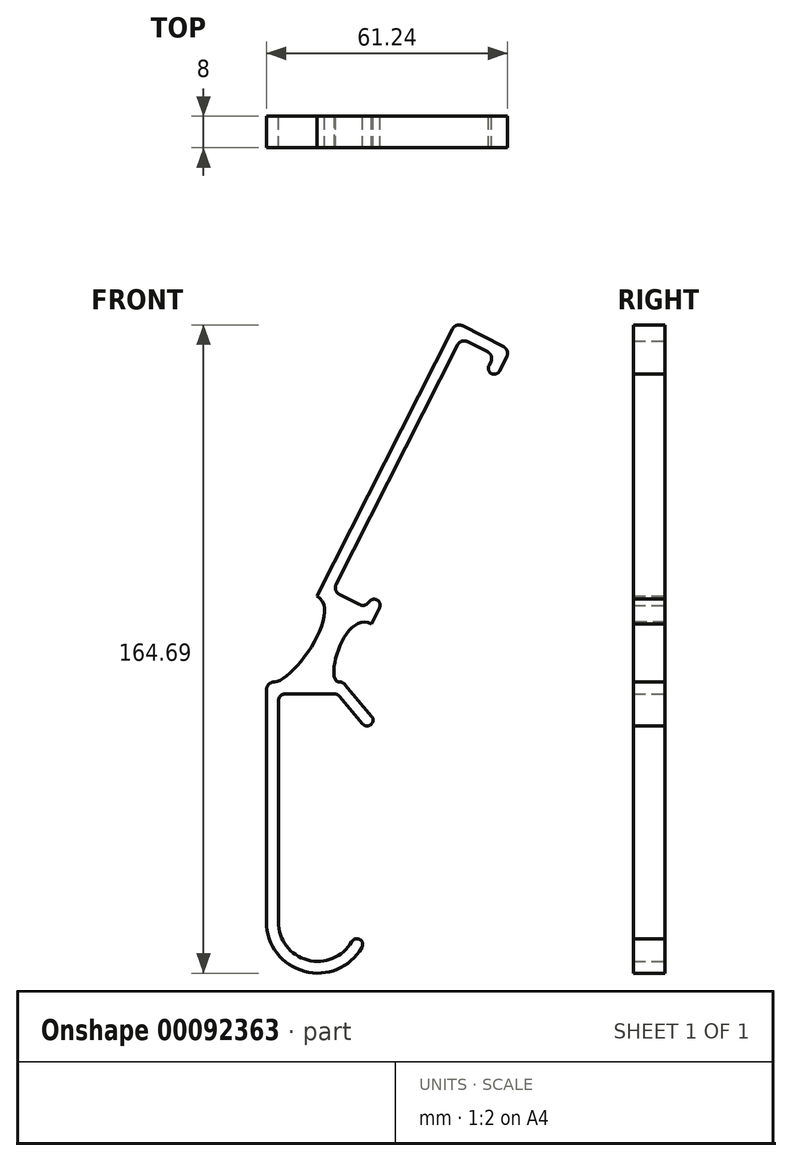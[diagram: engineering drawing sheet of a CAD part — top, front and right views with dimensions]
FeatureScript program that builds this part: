
annotation { "Feature Type Name" : "Feature", "Feature Type Description" : "" }
export const myFeature = defineFeature(function(context is Context, id is Id, definition is map)
    precondition{}
    {
        {
            var Q0;
            Q0=qCreatedBy(makeId("Front.planeOp"),FACE);
            var sketch = newSketch(context, id + "F0", { "sketchPlane" : qUnion([Q0])});
            skLineSegment(sketch, "E0", {"start": v(0, -2) * mm, "end": v(0, -58) * mm});
            skLineSegment(sketch, "E1", {"start": v(2, 0) * mm, "end": v(14.07, 0) * mm});
            skLineSegment(sketch, "E2", {"start": v(15.6, -0.71) * mm, "end": v(21.43, -7.66) * mm});
            skArc(sketch, "E3", {"start": v(0, -58) * mm, "mid": v(7.41, -67.66) * mm, "end": v(18.66, -63) * mm});
            skArc(sketch, "E4.0", {"start": v(-3, -58) * mm, "mid": v(6.64, -70.56) * mm, "end": v(21.26, -64.5) * mm});
            skLineSegment(sketch, "E4.1", {"start": v(-3, 1) * mm, "end": v(-3, -58) * mm});
            skLineSegment(sketch, "E4.2", {"start": v(-1, 3) * mm, "end": v(15.47, 3) * mm});
            skLineSegment(sketch, "E4.3", {"start": v(17, 2.29) * mm, "end": v(23.73, -5.73) * mm});
            skArc(sketch, "E5", {"start": v(21.43, -7.66) * mm, "mid": v(23.54, -7.85) * mm, "end": v(23.73, -5.73) * mm});
            skArc(sketch, "E6", {"start": v(21.26, -64.5) * mm, "mid": v(20.7, -62.45) * mm, "end": v(18.66, -63) * mm});
            skPoint(sketch, "E7.visualSharp", {"position": v(0, 0) * mm});
            skArc(sketch, "E7.filletArc", {"start": v(2, 0) * mm, "mid": v(0.59, -0.59) * mm, "end": v(0, -2) * mm});
            skPoint(sketch, "E8.visualSharp", {"position": v(15, 0) * mm});
            skArc(sketch, "E8.filletArc", {"start": v(15.6, -0.71) * mm, "mid": v(14.91, -0.19) * mm, "end": v(14.07, 0) * mm});
            skArc(sketch, "E9.filletArc", {"start": v(17, 2.29) * mm, "mid": v(16.31, 2.81) * mm, "end": v(15.47, 3) * mm});
            skPoint(sketch, "E10.visualSharp", {"position": v(-3, 3) * mm});
            skArc(sketch, "E10.filletArc", {"start": v(-1, 3) * mm, "mid": v(-2.41, 2.41) * mm, "end": v(-3, 1) * mm});
            skLineSegment(sketch, "E11", {"start": v(15.47, 3) * mm, "end": v(22.3, 21.8) * mm, "construction": true});
            skLineSegment(sketch, "E12", {"start": v(20.62, 22.65) * mm, "end": v(15.53, 25.23) * mm});
            skLineSegment(sketch, "E13", {"start": v(14.7, 27.78) * mm, "end": v(45.53, 88.61) * mm});
            skLineSegment(sketch, "E14", {"start": v(48.09, 89.45) * mm, "end": v(53.17, 86.87) * mm});
            skLineSegment(sketch, "E15", {"start": v(54, 84.32) * mm, "end": v(53.5, 83.34) * mm});
            skLineSegment(sketch, "E16.0", {"start": v(58.04, 85.64) * mm, "end": v(56.18, 81.98) * mm});
            skLineSegment(sketch, "E16.1", {"start": v(23.63, 17.76) * mm, "end": v(25.69, 21.83) * mm});
            skLineSegment(sketch, "E16.2", {"start": v(23.63, 17.76) * mm, "end": v(9.8, 24.77) * mm});
            skLineSegment(sketch, "E16.3", {"start": v(9.8, 24.77) * mm, "end": v(44.21, 92.65) * mm});
            skLineSegment(sketch, "E16.4", {"start": v(46.77, 93.48) * mm, "end": v(57.2, 88.2) * mm});
            skArc(sketch, "E17", {"start": v(53.5, 83.34) * mm, "mid": v(54.17, 81.32) * mm, "end": v(56.18, 81.98) * mm});
            skArc(sketch, "E18", {"start": v(25.69, 21.83) * mm, "mid": v(25.1, 23.8) * mm, "end": v(23.08, 23.32) * mm});
            skPoint(sketch, "E19.visualSharp", {"position": v(13.83, 26.09) * mm});
            skArc(sketch, "E19.filletArc", {"start": v(14.7, 27.78) * mm, "mid": v(14.58, 26.33) * mm, "end": v(15.53, 25.23) * mm});
            skPoint(sketch, "E20.visualSharp", {"position": v(22.3, 21.8) * mm});
            skArc(sketch, "E20.filletArc", {"start": v(20.62, 22.65) * mm, "mid": v(21.98, 22.5) * mm, "end": v(23.08, 23.32) * mm});
            skPoint(sketch, "E21.visualSharp", {"position": v(54.86, 86.01) * mm});
            skArc(sketch, "E21.filletArc", {"start": v(54, 84.32) * mm, "mid": v(54.12, 85.77) * mm, "end": v(53.17, 86.87) * mm});
            skPoint(sketch, "E22.visualSharp", {"position": v(46.4, 90.3) * mm});
            skArc(sketch, "E22.filletArc", {"start": v(48.09, 89.45) * mm, "mid": v(46.64, 89.56) * mm, "end": v(45.53, 88.61) * mm});
            skPoint(sketch, "E23.visualSharp", {"position": v(45.07, 94.34) * mm});
            skArc(sketch, "E23.filletArc", {"start": v(46.77, 93.48) * mm, "mid": v(45.32, 93.6) * mm, "end": v(44.21, 92.65) * mm});
            skPoint(sketch, "E24.visualSharp", {"position": v(58.9, 87.33) * mm});
            skArc(sketch, "E24.filletArc", {"start": v(58.04, 85.64) * mm, "mid": v(58.15, 87.09) * mm, "end": v(57.2, 88.2) * mm});
            skFitSpline(sketch, "E25", {"points": [v(9.8, 24.77) * mm, v(-1, 3) * mm], "startDerivative": vector(20.74, -10.51) * mm, "endDerivative": vector(-14.4, 0) * mm});
            skFitSpline(sketch, "E26", {"points": [v(23.63, 17.76) * mm, v(15.47, 3) * mm], "startDerivative": vector(-20.74, 10.51) * mm, "endDerivative": vector(11.8, 0) * mm});
            skSolve(sketch);
        }
        {
            var Q0;
            Q0=makeQuery(id+"F0.imprint","IMPRINT",FACE,{"disambiguationData":[TD([[makeQuery(id+"F0.imprint","IMPRINT",EDGE,{"derivedFrom":sQuery(id+"F0.wireOp",EDGE,"E0")}),-1.0]])]});
            var Q1;
            Q1=makeQuery(id+"F0.imprint","IMPRINT",FACE,{"disambiguationData":[TD([[makeQuery(id+"F0.imprint","IMPRINT",EDGE,{"derivedFrom":sQuery(id+"F0.wireOp",EDGE,"E4.2")}),1.0]])]});
            var Q2;
            Q2=makeQuery(id+"F0.imprint","IMPRINT",FACE,{"disambiguationData":[TD([[makeQuery(id+"F0.imprint","IMPRINT",EDGE,{"derivedFrom":sQuery(id+"F0.wireOp",EDGE,"E12")}),1.0]])]});
            extrude(context, id + "F1", {"entities" : qUnion([Q0, Q1, Q2]), "endBound" : BoundingType.SYMMETRIC, "depth" : 8 * mm});
        }
    });
